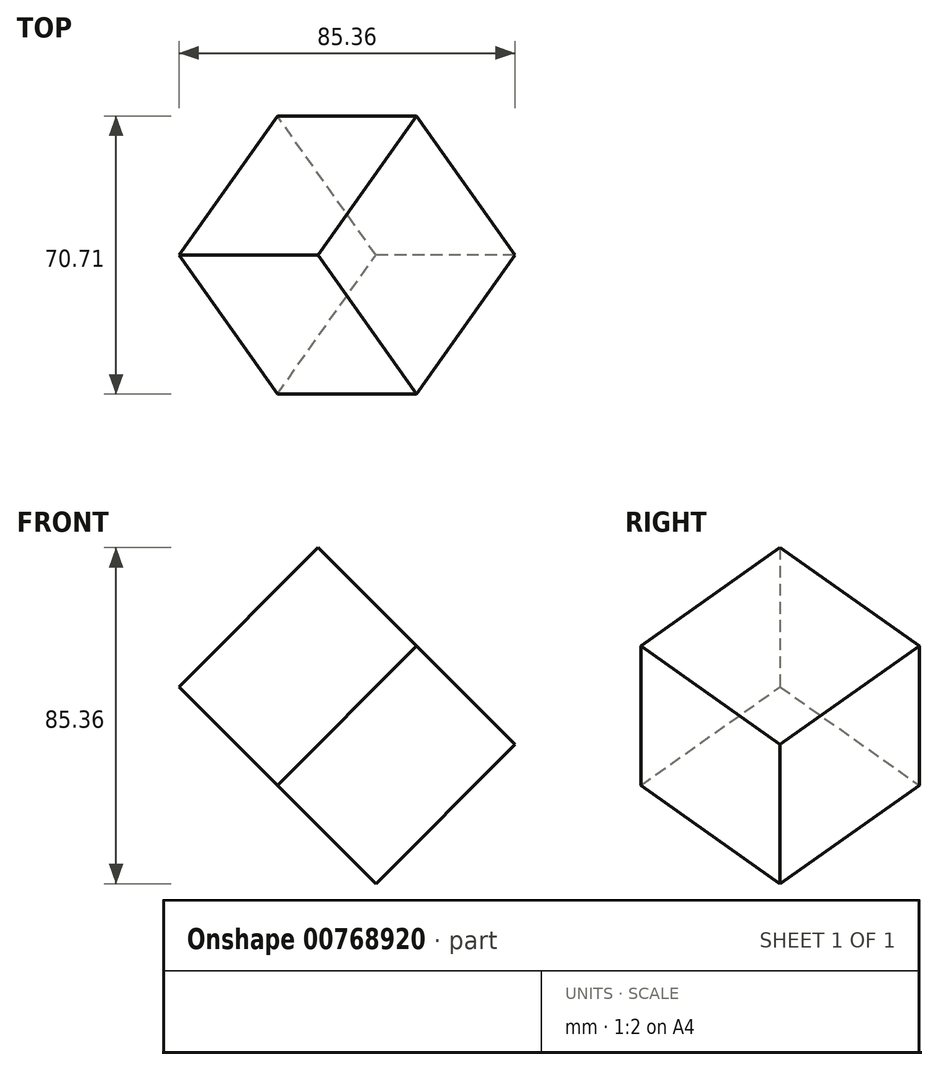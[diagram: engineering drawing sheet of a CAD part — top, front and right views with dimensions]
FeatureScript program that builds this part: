
annotation { "Feature Type Name" : "Feature", "Feature Type Description" : "" }
export const myFeature = defineFeature(function(context is Context, id is Id, definition is map)
    precondition{}
    {
        {
            var Q0;
            Q0=qCreatedBy(makeId("Top.planeOp"),FACE);
            var sketch = newSketch(context, id + "F0", { "sketchPlane" : qUnion([Q0])});
            skLineSegment(sketch, "E0.bottom", {"start": v(25, -25) * mm, "end": v(-25, -25) * mm});
            skLineSegment(sketch, "E0.top", {"start": v(25, 25) * mm, "end": v(-25, 25) * mm});
            skLineSegment(sketch, "E0.left", {"start": v(25, -25) * mm, "end": v(25, 25) * mm});
            skLineSegment(sketch, "E0.right", {"start": v(-25, -25) * mm, "end": v(-25, 25) * mm});
            skPoint(sketch, "E0.middle", {"position": v(0, 0) * mm});
            skSolve(sketch);
        }
        {
            var Q0;
            Q0=makeQuery(id+"F0.imprint","IMPRINT",FACE,{"disambiguationData":[TD([[makeQuery(id+"F0.imprint","IMPRINT",EDGE,{"derivedFrom":sQuery(id+"F0.wireOp",EDGE,"E0.bottom")}),-1.0]])]});
            extrude(context, id + "F1", {"entities" : qUnion([Q0]), "depth" : 50 * mm, "offsetDistance" : 25 * mm});
        }
        {
            var Q0;
            Q0=makeQuery(id+"F1.opExtrude","SWEPT_BODY",BODY,{"disambiguationData":[OSD([sQuery(id+"F0.wireOp",EDGE,"E0.bottom"),sQuery(id+"F0.wireOp",EDGE,"E0.top"),sQuery(id+"F0.wireOp",EDGE,"E0.left"),sQuery(id+"F0.wireOp",EDGE,"E0.right")])]});
            transform(context, id + "F2", {"entities" : qUnion([Q0]), "transformType" : TransformType.TRANSLATION_3D, "dx" : 0 * mm, "dy" : 0 * mm, "dz" : -25 * mm, "makeCopy" : false});
        }
        {
            var Q0;
            Q0=makeQuery(id+"F1.opExtrude","SWEPT_BODY",BODY,{"disambiguationData":[OSD([sQuery(id+"F0.wireOp",EDGE,"E0.bottom"),sQuery(id+"F0.wireOp",EDGE,"E0.top"),sQuery(id+"F0.wireOp",EDGE,"E0.left"),sQuery(id+"F0.wireOp",EDGE,"E0.right")])]});
            var Q1;
            Q1=makeQuery(id+"F1.opExtrude","SWEPT_EDGE",EDGE,{"disambiguationData":[OSD([sQuery(id+"F0.wireOp",EDGE,"E0.bottom"),sQuery(id+"F0.wireOp",EDGE,"E0.left")])]});
            transform(context, id + "F3", {"entities" : qUnion([Q0]), "transformType" : TransformType.ROTATION, "transformAxis" : qUnion([Q1]), "angle" : 45 * degree, "makeCopy" : false});
        }
        {
            var Q0;
            Q0=qCreatedBy(makeId("Top.planeOp"),FACE);
            var sketch = newSketch(context, id + "F4", { "sketchPlane" : qUnion([Q0])});
            skLineSegment(sketch, "E1", {"start": v(0, 0) * mm, "end": v(0, 41.46) * mm});
            skSolve(sketch);
        }
        {
            var Q0;
            Q0=makeQuery(id+"F1.opExtrude","SWEPT_BODY",BODY,{"disambiguationData":[OSD([sQuery(id+"F0.wireOp",EDGE,"E0.bottom"),sQuery(id+"F0.wireOp",EDGE,"E0.top"),sQuery(id+"F0.wireOp",EDGE,"E0.left"),sQuery(id+"F0.wireOp",EDGE,"E0.right")])]});
            var Q1;
            Q1=sQuery(id+"F4.wireOp",EDGE,"E1");
            transform(context, id + "F5", {"entities" : qUnion([Q0]), "transformType" : TransformType.ROTATION, "transformAxis" : qUnion([Q1]), "angle" : 45 * degree, "makeCopy" : false});
        }
    });
